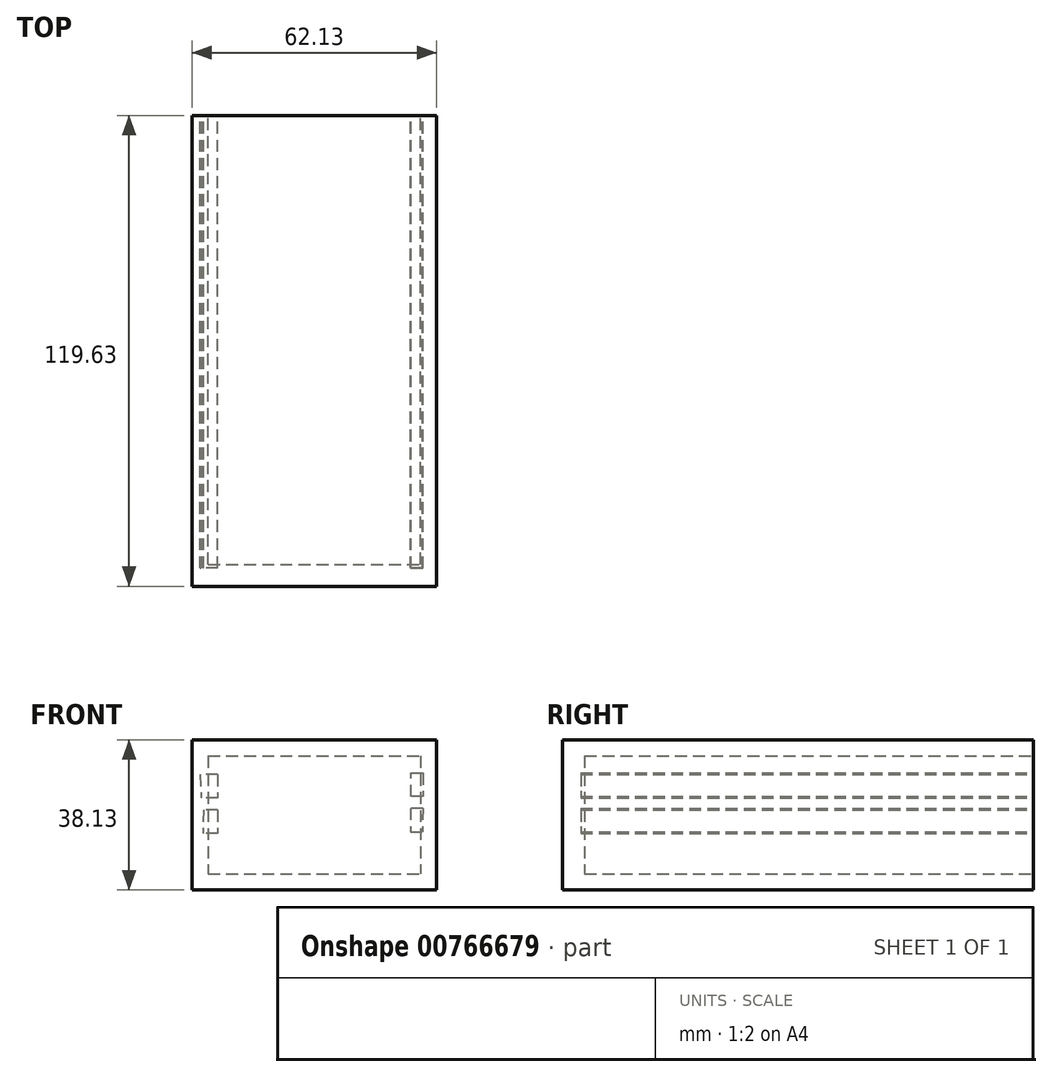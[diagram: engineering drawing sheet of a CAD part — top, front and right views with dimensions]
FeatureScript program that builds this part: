
annotation { "Feature Type Name" : "Feature", "Feature Type Description" : "" }
export const myFeature = defineFeature(function(context is Context, id is Id, definition is map)
    precondition{}
    {
        {
            var Q0;
            Q0=qCreatedBy(makeId("Front.planeOp"),FACE);
            var sketch = newSketch(context, id + "F0", { "sketchPlane" : qUnion([Q0])});
            skLineSegment(sketch, "E0.bottom", {"start": v(-32.36, 2) * mm, "end": v(21.64, 2) * mm});
            skLineSegment(sketch, "E0.top", {"start": v(-32.36, -28) * mm, "end": v(21.64, -28) * mm});
            skLineSegment(sketch, "E0.left", {"start": v(-32.36, 2) * mm, "end": v(-32.36, -28) * mm});
            skLineSegment(sketch, "E0.right", {"start": v(21.64, 2) * mm, "end": v(21.64, -28) * mm});
            skSolve(sketch);
        }
        {
            var Q0;
            Q0=makeQuery(id+"F0.imprint","IMPRINT",FACE,{"disambiguationData":[TD([[makeQuery(id+"F0.imprint","IMPRINT",EDGE,{"derivedFrom":sQuery(id+"F0.wireOp",EDGE,"E0.bottom")}),-1.0]])]});
            extrude(context, id + "F1", {"entities" : qUnion([Q0]), "depth" : 115 * mm, "offsetDistance" : 25.4 * mm});
        }
        {
            var Q0;
            Q0=qCreatedBy(makeId("Front.planeOp"),FACE);
            var sketch = newSketch(context, id + "F2", { "sketchPlane" : qUnion([Q0])});
            skLineSegment(sketch, "E1.bottom", {"start": v(25.7, 6.06) * mm, "end": v(-36.42, 6.06) * mm});
            skLineSegment(sketch, "E1.top", {"start": v(25.7, -32.07) * mm, "end": v(-36.42, -32.07) * mm});
            skLineSegment(sketch, "E1.left", {"start": v(25.7, 6.06) * mm, "end": v(25.7, -32.07) * mm});
            skLineSegment(sketch, "E1.right", {"start": v(-36.42, 6.06) * mm, "end": v(-36.42, -32.07) * mm});
            skSolve(sketch);
        }
        {
            var Q0;
            Q0=makeQuery(id+"F2.imprint","IMPRINT",FACE,{"disambiguationData":[TD([[makeQuery(id+"F2.imprint","IMPRINT",EDGE,{"derivedFrom":sQuery(id+"F2.wireOp",EDGE,"E1.bottom")}),1.0]])]});
            extrude(context, id + "F3", {"entities" : qUnion([Q0]), "operationType" : NewBodyOperationType.ADD, "depth" : 119.63 * mm, "offsetDistance" : 25.4 * mm});
        }
        {
            var Q0;
            Q0 = qSketchRegion(id + "F0", true);
            extrude(context, id + "F4", {"entities" : qUnion([Q0]), "operationType" : NewBodyOperationType.REMOVE, "oppositeDirection" : true, "depth" : 25.4 * mm, "offsetDistance" : 25.4 * mm});
        }
        {
            var Q0;
            Q0 = qSketchRegion(id + "F0", true);
            extrude(context, id + "F5", {"entities" : qUnion([Q0]), "operationType" : NewBodyOperationType.REMOVE, "depth" : 114.05 * mm, "offsetDistance" : 25.4 * mm});
        }
        {
            var Q0;
            Q0=qCreatedBy(makeId("Front.planeOp"),FACE);
            var sketch = newSketch(context, id + "F6", { "sketchPlane" : qUnion([Q0])});
            skLineSegment(sketch, "E2", {"start": v(22.2, -11.33) * mm, "end": v(19.04, -11.33) * mm});
            skLineSegment(sketch, "E3", {"start": v(19.04, -11.33) * mm, "end": v(19.04, -17.33) * mm});
            skLineSegment(sketch, "E4", {"start": v(19.04, -17.33) * mm, "end": v(22.09, -17.33) * mm});
            skLineSegment(sketch, "E5", {"start": v(22.32, -8.33) * mm, "end": v(19.27, -8.33) * mm});
            skLineSegment(sketch, "E6", {"start": v(19.27, -8.33) * mm, "end": v(19.27, -2.33) * mm});
            skLineSegment(sketch, "E7", {"start": v(19.27, -2.33) * mm, "end": v(22.21, -2.33) * mm});
            skLineSegment(sketch, "E8", {"start": v(-29.91, -2.74) * mm, "end": v(-29.91, -8.74) * mm});
            skLineSegment(sketch, "E9", {"start": v(-29.91, -11.74) * mm, "end": v(-29.91, -17.74) * mm});
            skLineSegment(sketch, "E10", {"start": v(-29.91, -2.74) * mm, "end": v(-34.38, -2.74) * mm});
            skLineSegment(sketch, "E11", {"start": v(-29.91, -8.74) * mm, "end": v(-34.11, -8.74) * mm});
            skLineSegment(sketch, "E12", {"start": v(-29.91, -11.74) * mm, "end": v(-33.5, -11.74) * mm});
            skLineSegment(sketch, "E13", {"start": v(-29.91, -17.74) * mm, "end": v(-33.6, -17.74) * mm});
            skLineSegment(sketch, "E14", {"start": v(22.21, -2.33) * mm, "end": v(22.32, -8.33) * mm});
            skLineSegment(sketch, "E15", {"start": v(22.2, -11.33) * mm, "end": v(22.09, -17.33) * mm});
            skLineSegment(sketch, "E16", {"start": v(-34.38, -2.74) * mm, "end": v(-34.11, -8.74) * mm});
            skLineSegment(sketch, "E17", {"start": v(-33.5, -11.74) * mm, "end": v(-33.6, -17.74) * mm});
            skSolve(sketch);
        }
        {
            var Q0;
            Q0 = qSketchRegion(id + "F6", true);
            extrude(context, id + "F7", {"entities" : qUnion([Q0]), "depth" : 115 * mm, "offsetDistance" : 25.4 * mm});
        }
    });
